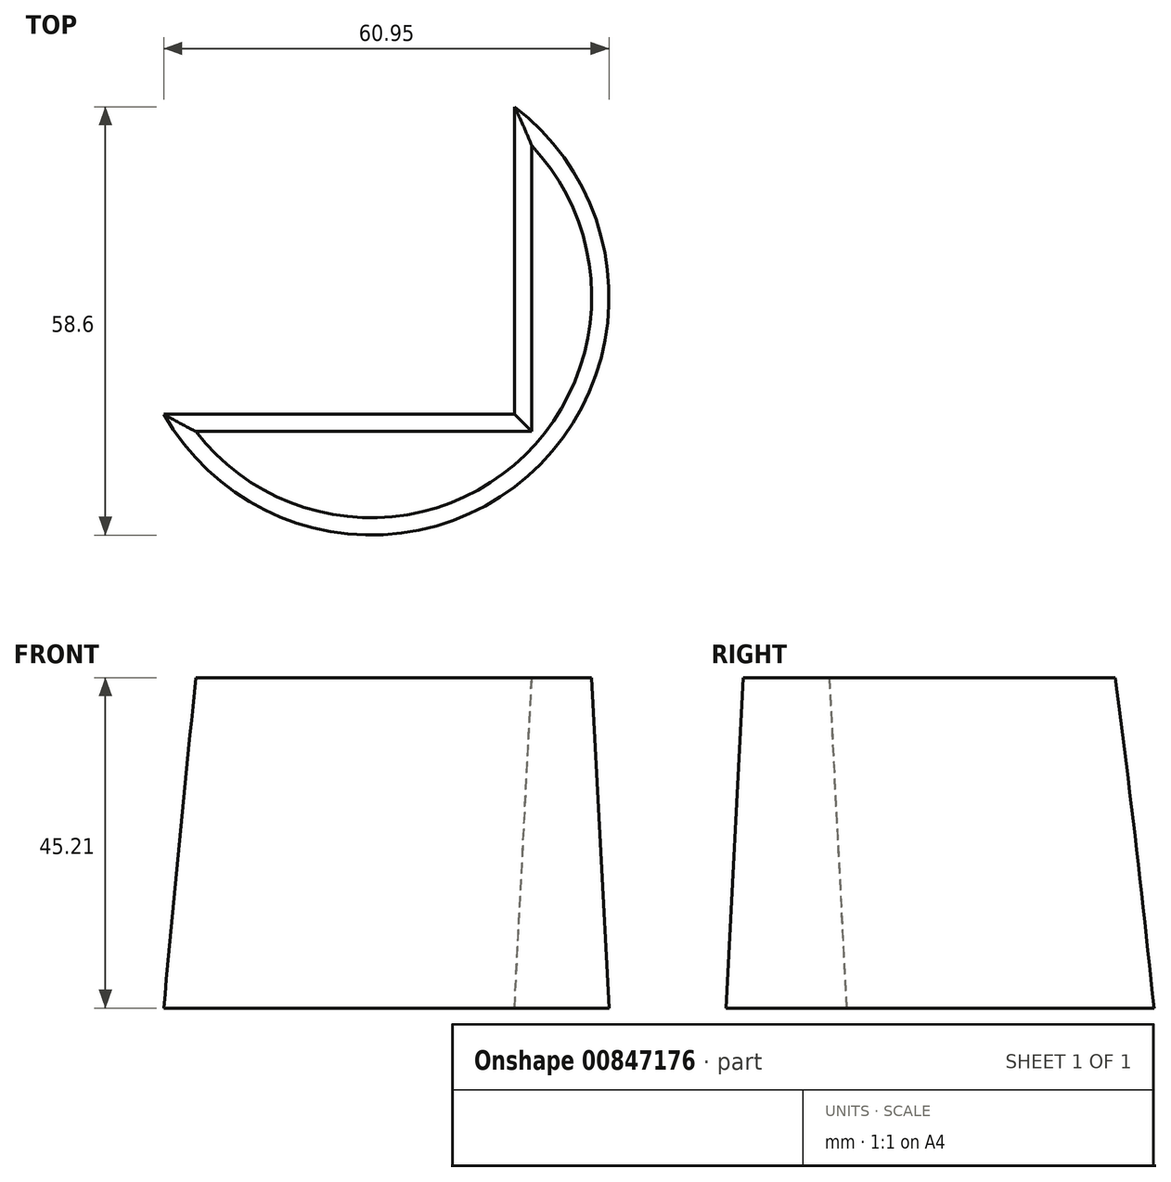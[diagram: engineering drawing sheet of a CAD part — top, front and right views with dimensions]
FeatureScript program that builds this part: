
annotation { "Feature Type Name" : "Feature", "Feature Type Description" : "" }
export const myFeature = defineFeature(function(context is Context, id is Id, definition is map)
    precondition{}
    {
        {
            var Q0;
            Q0=qCreatedBy(makeId("Top.planeOp"),FACE);
            var sketch = newSketch(context, id + "F0", { "sketchPlane" : qUnion([Q0])});
            skLineSegment(sketch, "E0.bottom", {"start": v(21.99, -33.08) * mm, "end": v(-23.96, -33.08) * mm});
            skLineSegment(sketch, "E0.top", {"start": v(21.99, 25.72) * mm, "end": v(-23.96, 25.72) * mm});
            skLineSegment(sketch, "E0.left", {"start": v(21.99, -33.08) * mm, "end": v(21.99, 25.72) * mm});
            skLineSegment(sketch, "E0.right", {"start": v(-23.96, -33.08) * mm, "end": v(-23.96, 25.72) * mm});
            skCircle(sketch, "E1", {"center": v(0, -14.66) * mm, "radius": 30.22 * mm});
            skSolve(sketch);
        }
        {
            var Q0;
            {var subQ0=sQuery(id+"F0.wireOp",EDGE,"E0.left");var subQ1=sQuery(id+"F0.wireOp",EDGE,"E0.bottom");var subQ2=makeQuery(id+"F0.imprint","INTERSECT",VERTEX,{"derivedFrom":[subQ1,subQ0]});Q0=makeQuery(id+"F0.imprint","IMPRINT",FACE,{"disambiguationData":[TD([[makeQuery(id+"F0.imprint","IMPRINT",EDGE,{"disambiguationData":[TD([[subQ2,-1.0]])],"derivedFrom":subQ1}),1.0]])]});}
            extrude(context, id + "F1", {"entities" : qUnion([Q0]), "oppositeDirection" : true, "depth" : 45.2 * mm, "offsetDistance" : 25.4 * mm, "hasDraft" : true, "draftAngle" : 3 * degree});
        }
    });
